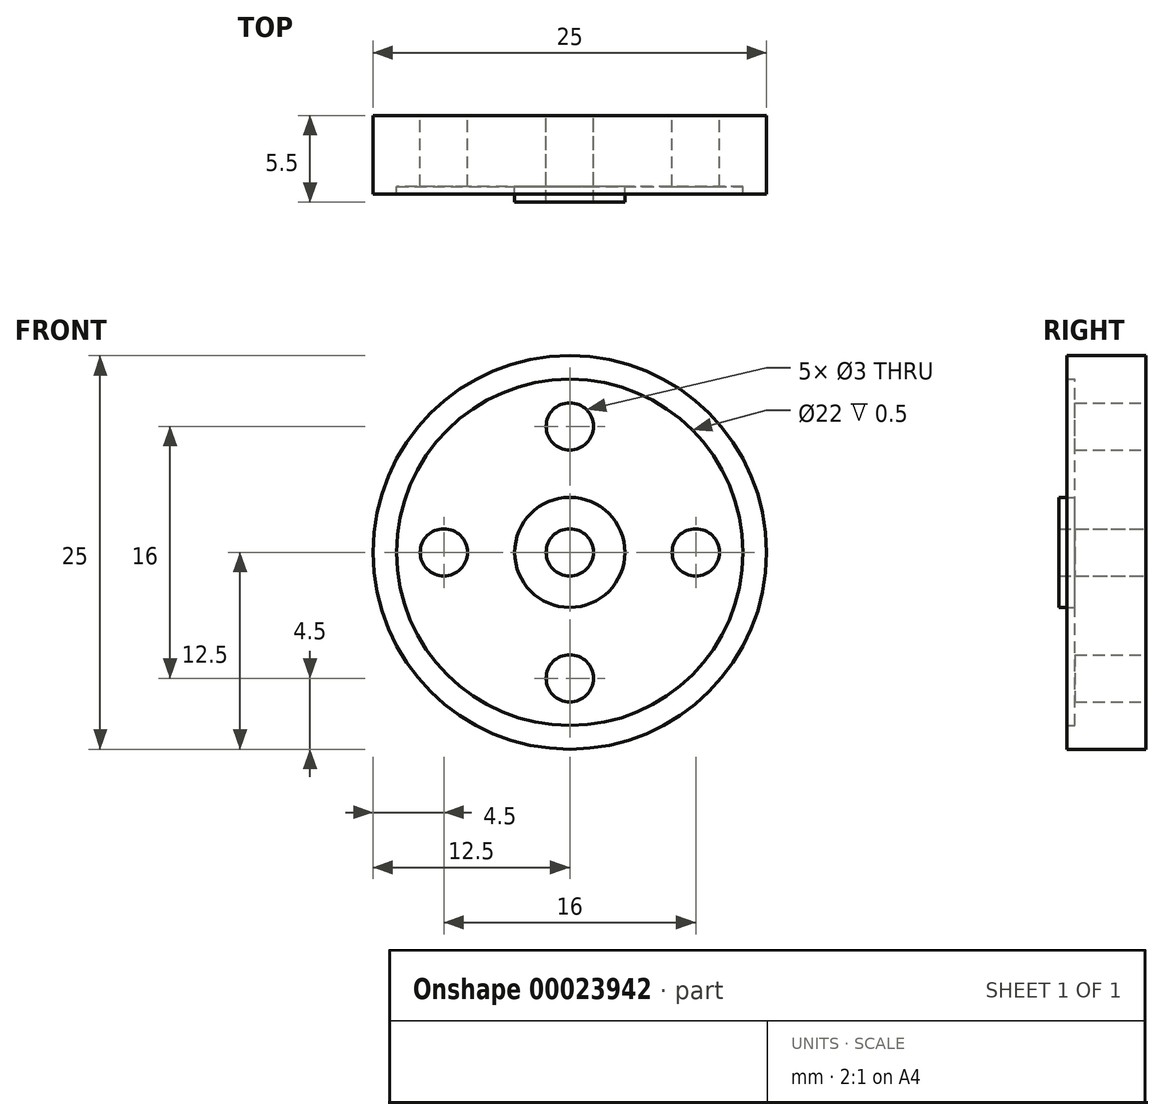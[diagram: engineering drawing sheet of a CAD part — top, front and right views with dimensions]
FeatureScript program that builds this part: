
annotation { "Feature Type Name" : "Feature", "Feature Type Description" : "" }
export const myFeature = defineFeature(function(context is Context, id is Id, definition is map)
    precondition{}
    {
        {
            var Q0;
            Q0=qCreatedBy(makeId("Front.planeOp"),FACE);
            var sketch = newSketch(context, id + "F0", { "sketchPlane" : qUnion([Q0])});
            skCircle(sketch, "E0", {"center": v(0, 0) * mm, "radius": 12.5 * mm});
            skCircle(sketch, "E1", {"center": v(0, 0) * mm, "radius": 3.5 * mm});
            skCircle(sketch, "E2", {"center": v(0, 0) * mm, "radius": 1.5 * mm});
            skCircle(sketch, "E3", {"center": v(0, 8) * mm, "radius": 1.5 * mm});
            skSolve(sketch);
        }
        {
            var Q0;
            Q0=makeQuery(id+"F0.imprint","IMPRINT",FACE,{"disambiguationData":[TD([[makeQuery(id+"F0.imprint","IMPRINT",EDGE,{"derivedFrom":sQuery(id+"F0.wireOp",EDGE,"E1")}),1.0]])]});
            extrude(context, id + "F1", {"entities" : qUnion([Q0]), "depth" : 5.5 * mm});
        }
        {
            var Q0;
            Q0=makeQuery(id+"F0.imprint","IMPRINT",FACE,{"disambiguationData":[TD([[makeQuery(id+"F0.imprint","IMPRINT",EDGE,{"derivedFrom":sQuery(id+"F0.wireOp",EDGE,"E0")}),1.0]])]});
            extrude(context, id + "F2", {"entities" : qUnion([Q0]), "operationType" : NewBodyOperationType.ADD, "depth" : 4.5 * mm});
        }
        {
            var Q0;
            Q0=makeQuery(id+"F2.opExtrude","SWEPT_FACE",FACE,{"disambiguationData":[OSD([sQuery(id+"F0.wireOp",EDGE,"E3")])]});
            var Q1;
            Q1=sQuery(id+"F0.wireOp",EDGE,"E0");
            circularPattern(context, id + "F3", {"faces" : qUnion([Q0]), "axis" : qUnion([Q1]), "angle" : 90 * degree, "instanceCount" : 4, "patternType" : PatternType.FACE});
        }
        {
            var Q0;
            Q0=makeQuery(id+"F2.opExtrude","CAP_FACE",FACE,{"disambiguationData":[OSD([sQuery(id+"F0.wireOp",EDGE,"E0"),sQuery(id+"F0.wireOp",EDGE,"E1"),sQuery(id+"F0.wireOp",EDGE,"E3")])],"isStart":false});
            var sketch = newSketch(context, id + "F4", { "sketchPlane" : qUnion([Q0])});
            skCircle(sketch, "E4", {"center": v(0, 0) * mm, "radius": 11 * mm});
            skSolve(sketch);
        }
        {
            var Q0;
            Q0=makeQuery(id+"F4.imprint","IMPRINT",FACE,{"disambiguationData":[TD([[makeQuery(id+"F4.imprint","IMPRINT",EDGE,{"derivedFrom":sQuery(id+"F4.wireOp",EDGE,"E4")}),-1.0]])]});
            extrude(context, id + "F5", {"entities" : qUnion([Q0]), "operationType" : NewBodyOperationType.ADD, "depth" : 0.5 * mm});
        }
    });
